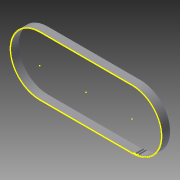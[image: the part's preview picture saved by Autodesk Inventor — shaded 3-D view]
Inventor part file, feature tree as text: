
AUTODESK INVENTOR PART (.ipt)
format: ipt  version: 2014 SP1 (Build 180222100, 222)  size: 156,160 bytes
history: native  units: in
note: dims shown in document units (in); Inventor stores cm internally (conversion verified against a paired STEP export)
features: other x3, sketch x1, imported_body x1
ambient origin geometry x8: Origin, YZ Plane, XZ Plane, XY Plane, X Axis, Y Axis, Z Axis, Center Point
bodies: Solid1 (feature_tree)
feature tree (5):
  other  "a6r25m1341501"
  sketch  "Sketch1"
  imported_body  "Base1"
  other  "Composite1"
  other  "Srf1"
